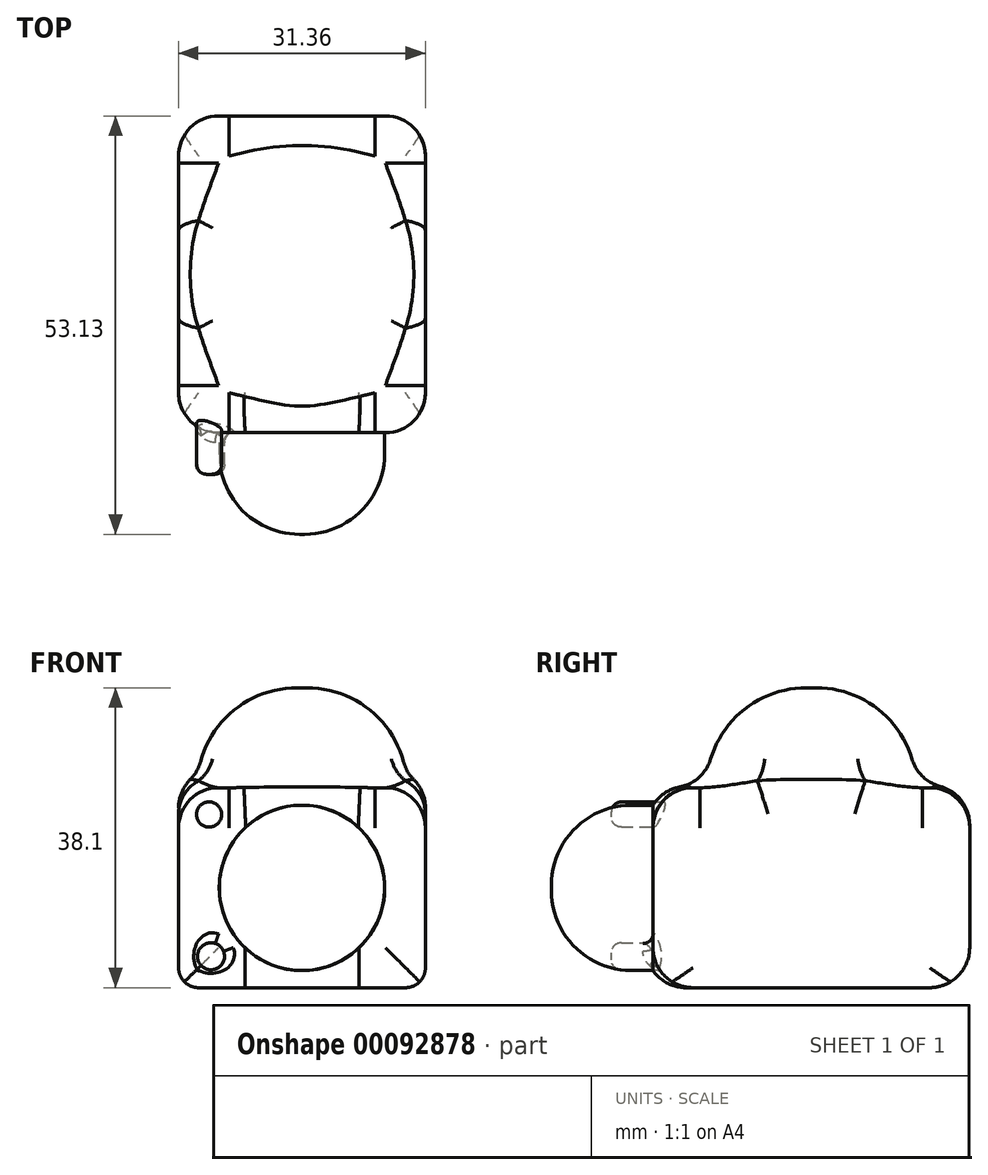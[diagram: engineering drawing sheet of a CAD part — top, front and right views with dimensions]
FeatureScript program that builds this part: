
annotation { "Feature Type Name" : "Feature", "Feature Type Description" : "" }
export const myFeature = defineFeature(function(context is Context, id is Id, definition is map)
    precondition{}
    {
        {
            var Q0;
            Q0=qCreatedBy(makeId("Top.planeOp"),FACE);
            var sketch = newSketch(context, id + "F0", { "sketchPlane" : qUnion([Q0])});
            skLineSegment(sketch, "E0.bottom", {"start": v(15.68, 20.11) * mm, "end": v(-15.68, 20.11) * mm});
            skLineSegment(sketch, "E0.top", {"start": v(15.68, -20.11) * mm, "end": v(-15.68, -20.11) * mm});
            skLineSegment(sketch, "E0.left", {"start": v(15.68, 20.11) * mm, "end": v(15.68, -20.11) * mm});
            skLineSegment(sketch, "E0.right", {"start": v(-15.68, 20.11) * mm, "end": v(-15.68, -20.11) * mm});
            skPoint(sketch, "E0.middle", {"position": v(0, 0) * mm});
            skCircle(sketch, "E1", {"center": v(0, 0) * mm, "radius": 13.33 * mm});
            skSolve(sketch);
        }
        {
            var Q0;
            Q0=makeQuery(id+"F0.imprint","IMPRINT",FACE,{"disambiguationData":[TD([[makeQuery(id+"F0.imprint","IMPRINT",EDGE,{"derivedFrom":sQuery(id+"F0.wireOp",EDGE,"E0.bottom")}),1.0]])]});
            extrude(context, id + "F1", {"entities" : qUnion([Q0]), "depth" : 25.4 * mm});
        }
        {
            var Q0;
            Q0=makeQuery(id+"F0.imprint","IMPRINT",FACE,{"disambiguationData":[TD([[makeQuery(id+"F0.imprint","IMPRINT",EDGE,{"derivedFrom":sQuery(id+"F0.wireOp",EDGE,"E1")}),1.0]])]});
            extrude(context, id + "F2", {"entities" : qUnion([Q0]), "operationType" : NewBodyOperationType.ADD, "depth" : 38.1 * mm});
        }
        {
            var Q0;
            Q0=makeQuery(id+"F2.opExtrude","CAP_EDGE",EDGE,{"disambiguationData":[OSD([sQuery(id+"F0.wireOp",EDGE,"E1")])],"isStart":false});
            fillet(context, id + "F3", {"entities" : qUnion([Q0]), "radius" : 12.7 * mm, "tangentPropagation" : true, "allowEdgeOverflow" : false});
        }
        {
            var Q0;
            Q0=qCreatedBy(makeId("Front.planeOp"),FACE);
            var sketch = newSketch(context, id + "F4", { "sketchPlane" : qUnion([Q0])});
            skCircle(sketch, "E2", {"center": v(0, 12.68) * mm, "radius": 10.5 * mm});
            skCircle(sketch, "E3", {"center": v(-11.8, 22) * mm, "radius": 1.6 * mm});
            skCircle(sketch, "E4", {"center": v(-11.56, 3.99) * mm, "radius": 1.72 * mm});
            skLineSegment(sketch, "E5", {"start": v(0, 40.46) * mm, "end": v(0, -9.57) * mm});
            skCircle(sketch, "E6.MirrorC", {"center": v(11.8, 22) * mm, "radius": 1.6 * mm});
            skCircle(sketch, "E7.MirrorC", {"center": v(11.56, 3.99) * mm, "radius": 1.72 * mm});
            skSolve(sketch);
        }
        {
            var Q0;
            Q0=makeQuery(id+"F4.imprint","IMPRINT",FACE,{"disambiguationData":[TD([[makeQuery(id+"F4.imprint","IMPRINT",EDGE,{"derivedFrom":sQuery(id+"F4.wireOp",EDGE,"E3")}),1.0]])]});
            var Q1;
            Q1=makeQuery(id+"F4.imprint","IMPRINT",FACE,{"disambiguationData":[TD([[makeQuery(id+"F4.imprint","IMPRINT",EDGE,{"derivedFrom":sQuery(id+"F4.wireOp",EDGE,"E6.MirrorC")}),-1.0]])]});
            var Q2;
            Q2=makeQuery(id+"F4.imprint","IMPRINT",FACE,{"disambiguationData":[TD([[makeQuery(id+"F4.imprint","IMPRINT",EDGE,{"derivedFrom":sQuery(id+"F4.wireOp",EDGE,"E4")}),1.0]])]});
            var Q3;
            Q3=makeQuery(id+"F4.imprint","IMPRINT",FACE,{"disambiguationData":[TD([[makeQuery(id+"F4.imprint","IMPRINT",EDGE,{"derivedFrom":sQuery(id+"F4.wireOp",EDGE,"E7.MirrorC")}),-1.0]])]});
            extrude(context, id + "F5", {"entities" : qUnion([Q0, Q1, Q2, Q3]), "operationType" : NewBodyOperationType.ADD, "depth" : 25.4 * mm});
        }
        {
            var Q0;
            {var subQ0=sQuery(id+"F4.wireOp",EDGE,"E5");var subQ1=sQuery(id+"F4.wireOp",EDGE,"E2");var subQ2=makeQuery(id+"F4.imprint","INTERSECT",VERTEX,{"disambiguationData":[OD(0.0)],"derivedFrom":[subQ1,subQ0]});Q0=makeQuery(id+"F4.imprint","IMPRINT",FACE,{"disambiguationData":[TD([[makeQuery(id+"F4.imprint","IMPRINT",EDGE,{"disambiguationData":[TD([[subQ2,1.0]])],"derivedFrom":subQ1}),1.0]])]});}
            var Q1;
            {var subQ0=sQuery(id+"F4.wireOp",EDGE,"E5");var subQ1=sQuery(id+"F4.wireOp",EDGE,"E2");var subQ2=makeQuery(id+"F4.imprint","INTERSECT",VERTEX,{"disambiguationData":[OD(0.0)],"derivedFrom":[subQ1,subQ0]});Q1=makeQuery(id+"F4.imprint","IMPRINT",FACE,{"disambiguationData":[TD([[makeQuery(id+"F4.imprint","IMPRINT",EDGE,{"disambiguationData":[TD([[subQ2,-1.0]])],"derivedFrom":subQ1}),1.0]])]});}
            extrude(context, id + "F6", {"entities" : qUnion([Q0, Q1]), "operationType" : NewBodyOperationType.ADD, "depth" : 33.02 * mm});
        }
        {
            var Q0;
            {var subQ0=sQuery(id+"F0.wireOp",EDGE,"E1");Q0=makeQuery(id+"F3.opFillet","BLEND_EDGE",EDGE,{"blendedFrom":[makeQuery(id+"F2.opExtrude","CAP_EDGE",EDGE,{"disambiguationData":[OSD([subQ0])],"isStart":false}),makeQuery(id+"F1.opExtrude","CAP_FACE",FACE,{"disambiguationData":[OSD([sQuery(id+"F0.wireOp",EDGE,"E0.bottom"),sQuery(id+"F0.wireOp",EDGE,"E0.top"),sQuery(id+"F0.wireOp",EDGE,"E0.left"),sQuery(id+"F0.wireOp",EDGE,"E0.right"),subQ0])],"isStart":false})],"blendedInto":[makeQuery(id+"F1.opExtrude","CAP_FACE",FACE,{"disambiguationData":[OSD([sQuery(id+"F0.wireOp",EDGE,"E0.bottom"),sQuery(id+"F0.wireOp",EDGE,"E0.top"),sQuery(id+"F0.wireOp",EDGE,"E0.left"),sQuery(id+"F0.wireOp",EDGE,"E0.right"),subQ0])],"isStart":false})]});}
            fillet(context, id + "F7", {"entities" : qUnion([Q0]), "radius" : 5.08 * mm, "tangentPropagation" : true, "allowEdgeOverflow" : false});
        }
        {
            var Q0;
            Q0=makeQuery(id+"F6.opExtrude","CAP_EDGE",EDGE,{"disambiguationData":[OSD([sQuery(id+"F4.wireOp",EDGE,"E2")])],"isStart":false});
            fillet(context, id + "F8", {"entities" : qUnion([Q0]), "radius" : 10.16 * mm, "tangentPropagation" : true, "allowEdgeOverflow" : false});
        }
        {
            var Q0;
            Q0=makeQuery(id+"F1.opExtrude","SWEPT_EDGE",EDGE,{"disambiguationData":[OSD([sQuery(id+"F0.wireOp",EDGE,"E0.top"),sQuery(id+"F0.wireOp",EDGE,"E0.right")])]});
            var Q1;
            Q1=makeQuery(id+"F1.opExtrude","CAP_EDGE",EDGE,{"disambiguationData":[OSD([sQuery(id+"F0.wireOp",EDGE,"E0.top")])],"isStart":false});
            var Q2;
            Q2=makeQuery(id+"F1.opExtrude","CAP_EDGE",EDGE,{"disambiguationData":[OSD([sQuery(id+"F0.wireOp",EDGE,"E0.top")])],"isStart":true});
            var Q3;
            Q3=makeQuery(id+"F1.opExtrude","SWEPT_EDGE",EDGE,{"disambiguationData":[OSD([sQuery(id+"F0.wireOp",EDGE,"E0.top"),sQuery(id+"F0.wireOp",EDGE,"E0.left")])]});
            var Q4;
            Q4=makeQuery(id+"F1.opExtrude","CAP_EDGE",EDGE,{"disambiguationData":[OSD([sQuery(id+"F0.wireOp",EDGE,"E0.left")])],"isStart":false});
            var Q5;
            Q5=makeQuery(id+"F1.opExtrude","CAP_EDGE",EDGE,{"disambiguationData":[OSD([sQuery(id+"F0.wireOp",EDGE,"E0.bottom")])],"isStart":false});
            var Q6;
            Q6=makeQuery(id+"F1.opExtrude","CAP_EDGE",EDGE,{"disambiguationData":[OSD([sQuery(id+"F0.wireOp",EDGE,"E0.right")])],"isStart":false});
            var Q7;
            Q7=makeQuery(id+"F1.opExtrude","SWEPT_EDGE",EDGE,{"disambiguationData":[OSD([sQuery(id+"F0.wireOp",EDGE,"E0.bottom"),sQuery(id+"F0.wireOp",EDGE,"E0.left")])]});
            var Q8;
            Q8=makeQuery(id+"F1.opExtrude","SWEPT_EDGE",EDGE,{"disambiguationData":[OSD([sQuery(id+"F0.wireOp",EDGE,"E0.bottom"),sQuery(id+"F0.wireOp",EDGE,"E0.right")])]});
            var Q9;
            Q9=makeQuery(id+"F1.opExtrude","CAP_EDGE",EDGE,{"disambiguationData":[OSD([sQuery(id+"F0.wireOp",EDGE,"E0.bottom")])],"isStart":true});
            fillet(context, id + "F9", {"entities" : qUnion([Q0, Q1, Q2, Q3, Q4, Q5, Q6, Q7, Q8, Q9]), "radius" : 5.08 * mm, "tangentPropagation" : true, "allowEdgeOverflow" : false});
        }
        {
            var Q0;
            Q0=makeQuery(id+"F5.opExtrude","CAP_EDGE",EDGE,{"disambiguationData":[OSD([sQuery(id+"F4.wireOp",EDGE,"E6.MirrorC")])],"isStart":false});
            var Q1;
            Q1=makeQuery(id+"F5.opExtrude","CAP_EDGE",EDGE,{"disambiguationData":[OSD([sQuery(id+"F4.wireOp",EDGE,"E7.MirrorC")])],"isStart":false});
            var Q2;
            Q2=makeQuery(id+"F5.opExtrude","CAP_EDGE",EDGE,{"disambiguationData":[OSD([sQuery(id+"F4.wireOp",EDGE,"E3")])],"isStart":false});
            var Q3;
            Q3=makeQuery(id+"F5.opExtrude","CAP_EDGE",EDGE,{"disambiguationData":[OSD([sQuery(id+"F4.wireOp",EDGE,"E4")])],"isStart":false});
            fillet(context, id + "F10", {"entities" : qUnion([Q0, Q1, Q2, Q3]), "radius" : 1.27 * mm, "tangentPropagation" : true, "allowEdgeOverflow" : false});
        }
        {
            var Q0;
            Q0=makeQuery(id+"F5.boolean.opBoolean","INTERSECT",EDGE,{"derivedFrom":[makeQuery(id+"F1.opExtrude","SWEPT_FACE",FACE,{"disambiguationData":[OSD([sQuery(id+"F0.wireOp",EDGE,"E0.top")])]}),makeQuery(id+"F5.opExtrude","SWEPT_FACE",FACE,{"disambiguationData":[OSD([sQuery(id+"F4.wireOp",EDGE,"E6.MirrorC")])]})]});
            var Q1;
            Q1=makeQuery(id+"F5.boolean.opBoolean","INTERSECT",EDGE,{"derivedFrom":[makeQuery(id+"F1.opExtrude","SWEPT_FACE",FACE,{"disambiguationData":[OSD([sQuery(id+"F0.wireOp",EDGE,"E0.top")])]}),makeQuery(id+"F5.opExtrude","SWEPT_FACE",FACE,{"disambiguationData":[OSD([sQuery(id+"F4.wireOp",EDGE,"E7.MirrorC")])]})]});
            var Q2;
            Q2=makeQuery(id+"F5.boolean.opBoolean","INTERSECT",EDGE,{"derivedFrom":[makeQuery(id+"F1.opExtrude","SWEPT_FACE",FACE,{"disambiguationData":[OSD([sQuery(id+"F0.wireOp",EDGE,"E0.top")])]}),makeQuery(id+"F5.opExtrude","SWEPT_FACE",FACE,{"disambiguationData":[OSD([sQuery(id+"F4.wireOp",EDGE,"E3")])]})]});
            var Q3;
            Q3=makeQuery(id+"F5.boolean.opBoolean","INTERSECT",EDGE,{"derivedFrom":[makeQuery(id+"F1.opExtrude","SWEPT_FACE",FACE,{"disambiguationData":[OSD([sQuery(id+"F0.wireOp",EDGE,"E0.top")])]}),makeQuery(id+"F5.opExtrude","SWEPT_FACE",FACE,{"disambiguationData":[OSD([sQuery(id+"F4.wireOp",EDGE,"E4")])]})]});
            fillet(context, id + "F11", {"entities" : qUnion([Q0, Q1, Q2, Q3]), "radius" : 1.27 * mm, "tangentPropagation" : true, "allowEdgeOverflow" : false});
        }
        {
            var Q0;
            Q0=makeQuery(id+"F1.opExtrude","CAP_EDGE",EDGE,{"disambiguationData":[OSD([sQuery(id+"F0.wireOp",EDGE,"E0.right")])],"isStart":true});
            var Q1;
            Q1=makeQuery(id+"F1.opExtrude","CAP_EDGE",EDGE,{"disambiguationData":[OSD([sQuery(id+"F0.wireOp",EDGE,"E0.left")])],"isStart":true});
            fillet(context, id + "F12", {"entities" : qUnion([Q0, Q1]), "radius" : 2.54 * mm, "allowEdgeOverflow" : false});
        }
    });
